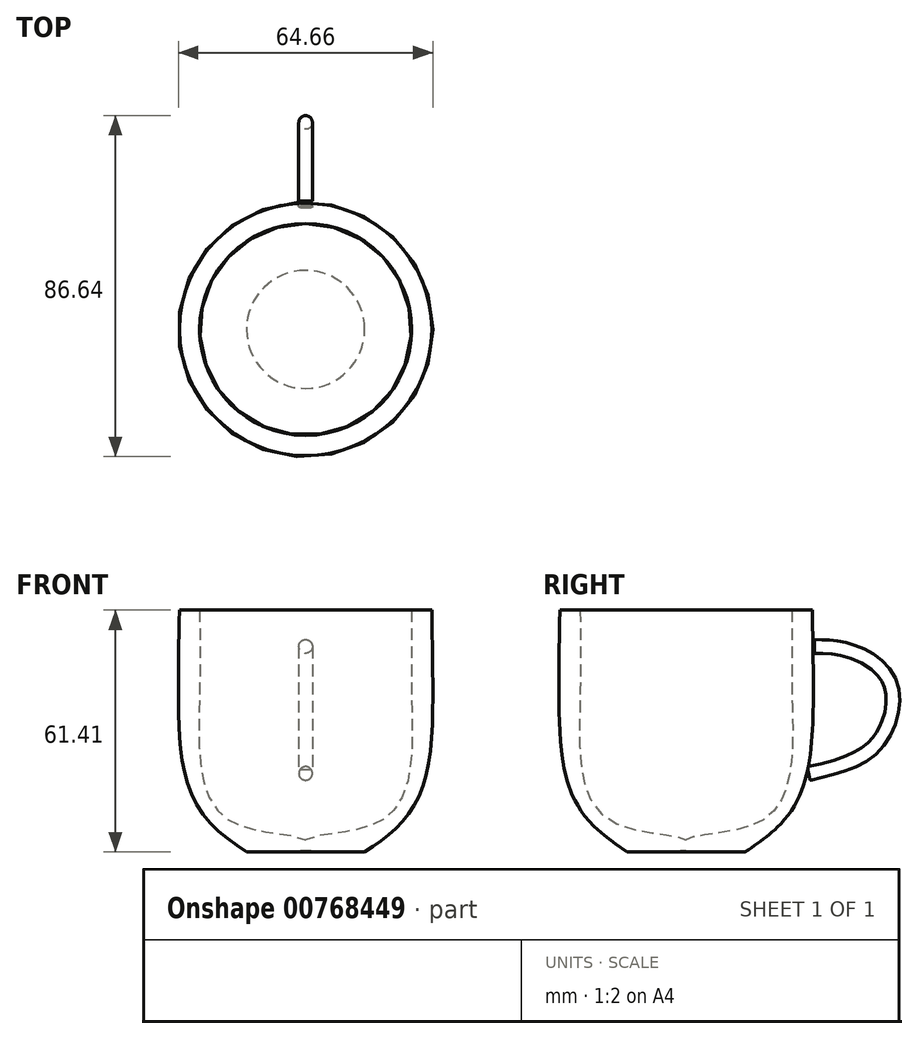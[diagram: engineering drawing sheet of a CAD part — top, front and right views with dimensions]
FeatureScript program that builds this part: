
annotation { "Feature Type Name" : "Feature", "Feature Type Description" : "" }
export const myFeature = defineFeature(function(context is Context, id is Id, definition is map)
    precondition{}
    {
        {
            var Q0;
            Q0=qCreatedBy(makeId("Right.planeOp"),FACE);
            var sketch = newSketch(context, id + "F0", { "sketchPlane" : qUnion([Q0])});
            skLineSegment(sketch, "E0", {"start": v(0, 75.33) * mm, "end": v(0, -75.33) * mm});
            skFitSpline(sketch, "E1", {"points": [v(0, -19.6) * mm, v(8.25, -19.88) * mm, v(15.01, -19.88) * mm, v(14.74, -20.15) * mm], "startDerivative": vector(15.8, -1.05) * mm, "endDerivative": vector(-4.59, -2.96) * mm});
            skFitSpline(sketch, "E2", {"points": [v(15.01, -19.88) * mm, v(24.48, -12.3) * mm, v(30.7, 0) * mm, v(32.32, 22.04) * mm, v(32.05, 41.52) * mm], "startDerivative": vector(47.5, 32.13) * mm, "endDerivative": vector(-1.4, 69.42) * mm});
            skFitSpline(sketch, "E3", {"points": [v(32.05, 41.52) * mm, v(26.91, 41.52) * mm, v(26.64, 41.52) * mm], "startDerivative": vector(-8.3, 0) * mm, "endDerivative": vector(-1, 0) * mm});
            skFitSpline(sketch, "E4", {"points": [v(26.91, 35.26) * mm, v(26.91, 41.52) * mm, v(26.91, 20.42) * mm, v(26.91, 5) * mm, v(19.6, -11.77) * mm, v(0, -16.9) * mm, v(0, -19.6) * mm], "startDerivative": vector(0.17, 84.28) * mm, "endDerivative": vector(15.8, -39.5) * mm});
            skSolve(sketch);
        }
        {
            var Q0;
            {var subQ1=sQuery(id+"F0.wireOp",EDGE,"E2");Q0=makeQuery(id+"F0.imprint","IMPRINT",FACE,{"disambiguationData":[TD([[makeQuery(id+"F0.imprint","IMPRINT",EDGE,{"derivedFrom":subQ1}),1.0]])]});}
            var Q1;
            Q1=sQuery(id+"F0.wireOp",EDGE,"E0");
            revolve(context, id + "F1", {"surfaceOperationType" : NewSurfaceOperationType.NEW, "entities" : qUnion([Q0]), "axis" : qUnion([Q1]), "revolveType" : RevolveType.FULL});
        }
        {
            var Q0;
            Q0=qCreatedBy(makeId("Right.planeOp"),FACE);
            var sketch = newSketch(context, id + "F2", { "sketchPlane" : qUnion([Q0])});
            skFitSpline(sketch, "E5", {"points": [v(32.6, 32.32) * mm, v(41.52, 31.24) * mm, v(51.8, 23.13) * mm, v(48.28, 7.44) * mm, v(31.17, 0) * mm], "startDerivative": vector(42.31, -0.57) * mm, "endDerivative": vector(-68.36, -15.12) * mm});
            skSolve(sketch);
        }
        {
            var Q0;
            Q0=sQuery(id+"F2.wireOp",VERTEX,"E5.start");
            var Q1;
            Q1=sQuery(id+"F2.wireOp",EDGE,"E5");
            cPlane(context, id + "F3", {"entities" : qUnion([Q0, Q1]), "cplaneType" : CPlaneType.CURVE_POINT, "offset" : 25 * mm, "width" : 150 * mm, "height" : 150 * mm});
        }
        {
            var Q0;
            Q0=qCreatedBy(id+"F3.planeOp",FACE);
            var sketch = newSketch(context, id + "F4", { "sketchPlane" : qUnion([Q0])});
            skCircle(sketch, "E6", {"center": v(0, 32.74) * mm, "radius": 1.74 * mm});
            skSolve(sketch);
        }
        {
            var Q0;
            Q0=makeQuery(id+"F4.imprint","IMPRINT",FACE,{"disambiguationData":[TD([[makeQuery(id+"F4.imprint","IMPRINT",EDGE,{"derivedFrom":sQuery(id+"F4.wireOp",EDGE,"E6")}),1.0]])]});
            var Q1;
            Q1=sQuery(id+"F2.wireOp",EDGE,"E5");
            sweep(context, id + "F5", {"operationType" : NewBodyOperationType.ADD, "profiles" : qUnion([Q0]), "path" : qUnion([Q1])});
        }
    });
